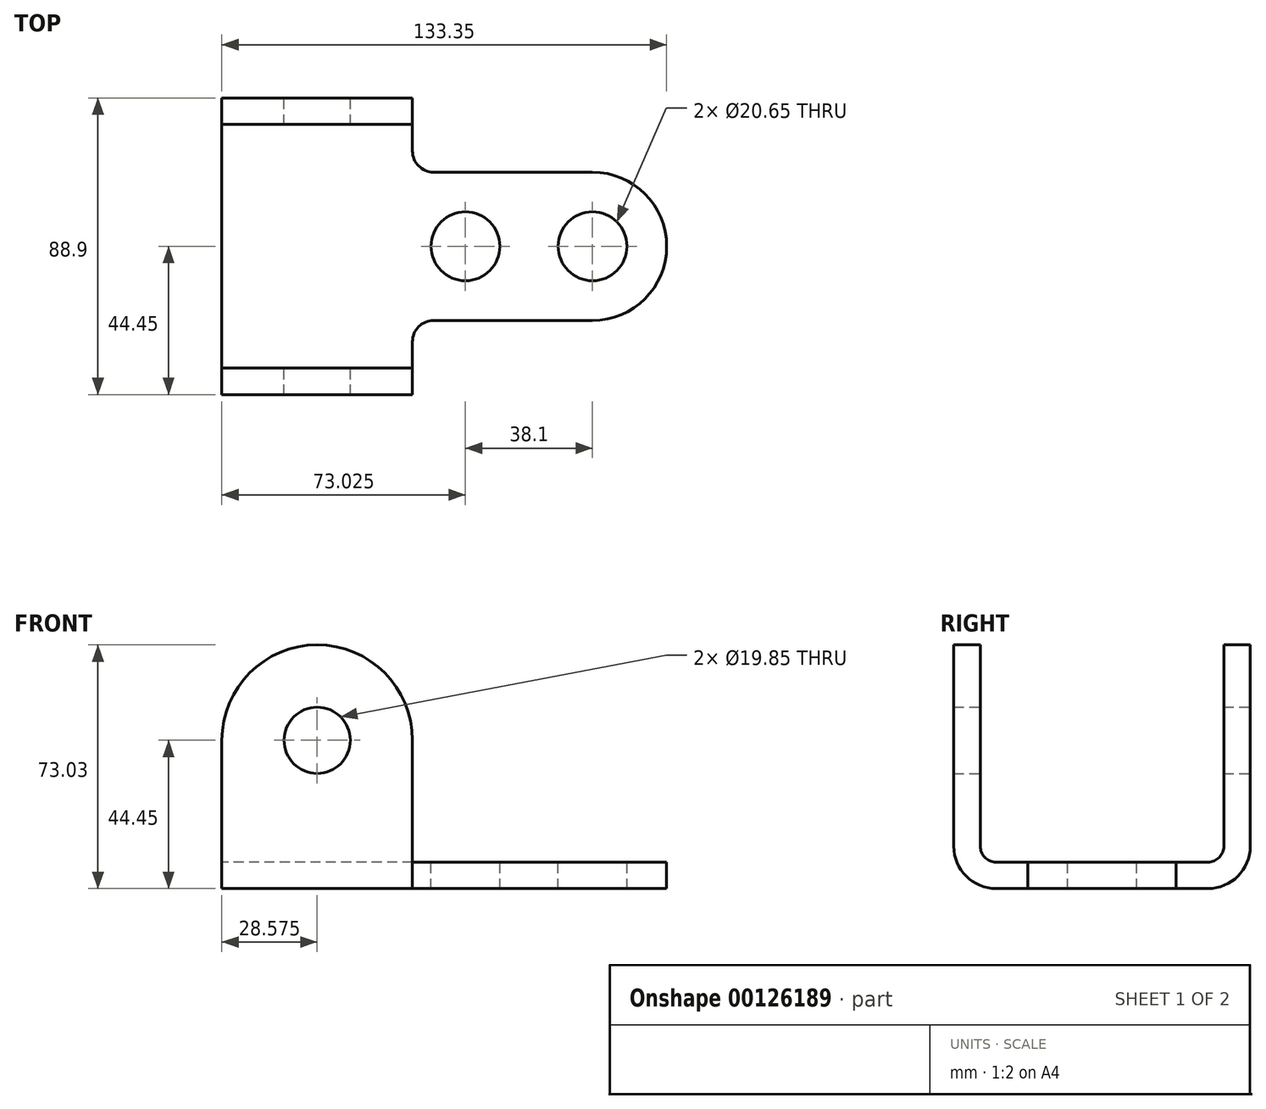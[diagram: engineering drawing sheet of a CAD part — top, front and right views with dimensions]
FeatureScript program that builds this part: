
annotation { "Feature Type Name" : "Feature", "Feature Type Description" : "" }
export const myFeature = defineFeature(function(context is Context, id is Id, definition is map)
    precondition{}
    {
        {
            var Q0;
            Q0=qCreatedBy(makeId("Front.planeOp"),FACE);
            var sketch = newSketch(context, id + "F0", { "sketchPlane" : qUnion([Q0])});
            skLineSegment(sketch, "E0", {"start": v(0, 0) * mm, "end": v(0, 44.45) * mm});
            skLineSegment(sketch, "E1", {"start": v(57.15, 44.45) * mm, "end": v(57.15, 0) * mm});
            skLineSegment(sketch, "E2", {"start": v(0, 0) * mm, "end": v(133.35, 0) * mm});
            skLineSegment(sketch, "E3", {"start": v(133.35, 0) * mm, "end": v(133.35, 7.94) * mm});
            skLineSegment(sketch, "E4", {"start": v(133.35, 7.94) * mm, "end": v(57.15, 7.94) * mm});
            skArc(sketch, "E5", {"start": v(57.15, 44.45) * mm, "mid": v(28.58, 73.03) * mm, "end": v(0, 44.45) * mm});
            skCircle(sketch, "E6", {"center": v(28.58, 44.45) * mm, "radius": 9.92 * mm});
            skSolve(sketch);
        }
        {
            var Q0;
            Q0 = qSketchRegion(id + "F0", true);
            extrude(context, id + "F1", {"entities" : qUnion([Q0]), "depth" : 88.9 * mm});
        }
        {
            var Q0;
            Q0=makeQuery(id+"F1.opExtrude","SWEPT_FACE",FACE,{"disambiguationData":[OSD([sQuery(id+"F0.wireOp",EDGE,"E4")])]});
            var sketch = newSketch(context, id + "F2", { "sketchPlane" : qUnion([Q0])});
            skCircle(sketch, "E7", {"center": v(73.03, -44.45) * mm, "radius": 10.33 * mm});
            skCircle(sketch, "E8", {"center": v(111.12, -44.45) * mm, "radius": 10.33 * mm});
            skLineSegment(sketch, "E9", {"start": v(57.15, 0) * mm, "end": v(57.15, -15.88) * mm});
            skLineSegment(sketch, "E10", {"start": v(57.15, -88.9) * mm, "end": v(57.15, -73.02) * mm});
            skArc(sketch, "E11", {"start": v(63.5, -66.67) * mm, "mid": v(59, -68.53) * mm, "end": v(57.15, -73.02) * mm});
            skArc(sketch, "E12", {"start": v(57.15, -15.88) * mm, "mid": v(59, -20.37) * mm, "end": v(63.5, -22.23) * mm});
            skLineSegment(sketch, "E13", {"start": v(63.5, -22.23) * mm, "end": v(111.13, -22.23) * mm});
            skLineSegment(sketch, "E14", {"start": v(63.5, -66.67) * mm, "end": v(111.13, -66.67) * mm});
            skArc(sketch, "E15", {"start": v(111.13, -66.68) * mm, "mid": v(133.35, -44.45) * mm, "end": v(111.13, -22.23) * mm});
            skLineSegment(sketch, "E16", {"start": v(57.15, 0) * mm, "end": v(133.35, 0) * mm});
            skLineSegment(sketch, "E17", {"start": v(57.15, -88.9) * mm, "end": v(133.35, -88.9) * mm});
            skLineSegment(sketch, "E18", {"start": v(57.15, -44.45) * mm, "end": v(194.7, -44.45) * mm, "construction": true});
            skPoint(sketch, "E18.endSnap0", {"position": v(133.35, -44.45) * mm});
            skLineSegment(sketch, "E19", {"start": v(133.35, 0) * mm, "end": v(133.35, -88.9) * mm});
            skSolve(sketch);
        }
        {
            var Q0;
            Q0 = qSketchRegion(id + "F2", true);
            extrude(context, id + "F3", {"entities" : qUnion([Q0]), "operationType" : NewBodyOperationType.REMOVE, "endBound" : BoundingType.THROUGH_ALL, "oppositeDirection" : true, "depth" : 25.4 * mm});
        }
        {
            var Q0;
            Q0=qCreatedBy(makeId("Right.planeOp"),FACE);
            var sketch = newSketch(context, id + "F4", { "sketchPlane" : qUnion([Q0])});
            skLineSegment(sketch, "E20", {"start": v(-80.96, 73.03) * mm, "end": v(-80.96, 12.7) * mm});
            skLineSegment(sketch, "E21", {"start": v(-76.2, 7.94) * mm, "end": v(-12.7, 7.94) * mm});
            skLineSegment(sketch, "E22", {"start": v(-7.94, 12.7) * mm, "end": v(-7.94, 73.03) * mm});
            skArc(sketch, "E23", {"start": v(-80.96, 12.7) * mm, "mid": v(-79.57, 9.33) * mm, "end": v(-76.2, 7.94) * mm});
            skArc(sketch, "E24", {"start": v(-12.7, 7.94) * mm, "mid": v(-9.33, 9.33) * mm, "end": v(-7.94, 12.7) * mm});
            skArc(sketch, "E25", {"start": v(-88.9, 12.7) * mm, "mid": v(-85.18, 3.72) * mm, "end": v(-76.2, 0) * mm});
            skLineSegment(sketch, "E26", {"start": v(-88.9, 12.7) * mm, "end": v(-88.9, 0) * mm});
            skLineSegment(sketch, "E27", {"start": v(-88.9, 0) * mm, "end": v(-76.2, 0) * mm});
            skLineSegment(sketch, "E28", {"start": v(-80.96, 73.03) * mm, "end": v(-7.94, 73.03) * mm});
            skLineSegment(sketch, "E29", {"start": v(0, 0) * mm, "end": v(0, 12.7) * mm});
            skLineSegment(sketch, "E30", {"start": v(0, 0) * mm, "end": v(-12.7, 0) * mm});
            skArc(sketch, "E31", {"start": v(-12.7, 0) * mm, "mid": v(-3.72, 3.72) * mm, "end": v(0, 12.7) * mm});
            skLineSegment(sketch, "E32", {"start": v(-44.45, 73.03) * mm, "end": v(-44.45, 0) * mm, "construction": true});
            skPoint(sketch, "E32.endSnap0", {"position": v(-44.45, 7.94) * mm});
            skSolve(sketch);
        }
        {
            var Q0;
            Q0 = qSketchRegion(id + "F4", true);
            extrude(context, id + "F5", {"entities" : qUnion([Q0]), "operationType" : NewBodyOperationType.REMOVE, "endBound" : BoundingType.THROUGH_ALL, "depth" : 25.4 * mm});
        }
    });
